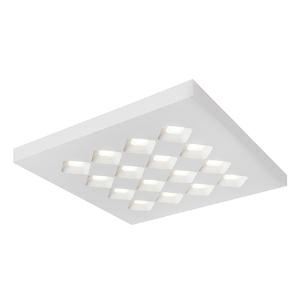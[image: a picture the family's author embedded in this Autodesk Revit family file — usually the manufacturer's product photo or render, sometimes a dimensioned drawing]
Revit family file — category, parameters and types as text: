
# Revit family: 3f_filippi_-_3f_diagon_p_soft_ugr_3f_filippi_-_12139_-_3f_diagon_p_39w-940_dali_soft_ugr_596x596
name_source: partatom
category: Lighting Fixtures
units: mm (PartAtom-declared; Revit-internal decimal feet)

## family parameters
Cut with Voids When Loaded = No
Host = Face
Light Source = No
Part Type = Normal
Room Calculation Point = No
Round Connector Dimension = Use Diameter
Shared = No

## types (1)
- 3F Filippi - 3F Dìagon P Soft UGR (1 x LED, 3890 lm, 40 W, 4000 K)
    Apparent Load = 40 VA
    Approval mark = CE
    CIE Flux Codes = 59 92 100 100 100
    Color Rendering = 90
    Color Temperature = 4000 K
    Control Gear = Electronic transformer
    Default Elevation = 1800 mm
    Description = ILLUMINOTECHNICAL
Luminous efficiency 100% (DLOR 100%, ULOR 0%).
Initial luminous flux of the luminaire 3890 lm.
Direct symmetric distribution.
Installation Interdistance Transv.D = 1.23 x hu - Long.D = 1.23 x hu.
Average luminance <3000 cd/m² for radial angles >65°.
Tabular UGR (CIE 117 - 4H-8H; S=0.25H; 70/50/20): RUG 18.9 - 18.9.
Beam angle: 102° - 101°.
Luminous efficacy 97 lm/W.
Lifetime (L90/B10): 30000 h. (tq+25°C)
Lifetime (L85/B10): 50000 h. (tq+25°C)
Lifetime (L80/B20): 80000 h. (tq+25°C)
Lifetime (L70/B20): 100000 h. (tq+25°C)
Sudden decreased luminous flux after 50000 hours: 0% (C0).
Photobiological safety in compliance with IEC/TR 62778: RG0 risk exempt, (IEC 62471).
In compliance with IEC/EN 62722-2-1 - IEC/EN 62717 standards.

SOURCE
Squared LED module 39W/940.
Energy efficiency class (UE 2019/2020 - UE 2019/2015): D.
CIE 13.3 Colour rendering index: CRI >90 (R9 >50%).
IES TM-30 Fidelity Index: Rf = 92 Rg = 101.
CCT nominal colour temperature 4000 K.
Colour initial tolerance (MacAdam): SDCM 3.

MECHANICAL
White painted frame.
Height only 40 mm.
Housing in hot-galvanised steel, painted in white polyester.
Honeycombed diagonal screen in white anti-glare polycarbonate.
Opal methacrylate (PMMA) rhomboid lenses with differentiated, engraved and prismatic surfaces for diffused, soft lighting and excellent visual comfort.
Luminaire with limited surface temperature. - D - (EN 60598-2-24)
Dimensions: 596x596 mm, height 40 mm. Weight 6.245 kg.
IP40 protection degree.
Mechanical strength to impacts IK06 (1 joule).
Glow-wire test resistance 650°C.

ELECTRICAL
Halogen Free DALI-2, PUSH-DIM, electronic wiring 230V-50/60Hz, power factor 0.97 at full load, THD <25%, constant output current, class I, 1 driver, 1 DALI addresse.
Power of the luminaire 40 W.
ENEC - CE.
SAFE FLICKER: PstLM=<1 and SVM=<0.4 (IEC TR 61547-1 and IEC TR 63158), to ensure a more comfortable and safe light.
Luminaire compliant with EN 60598-2-22 for power supply from a centralised emergency system CPSS (Central Power Supply System), not incorporated in the luminaire - high risk areas excluded. The default power and flux are 100% in AC and 15% in DC.
Ambient temperature from 0°C to +25°C.
Temperature class T6 max 85°C.
Quick connection.
Relative humidity UR: <85%.

INSTALLATION
Ceiling.

APPLICATIONS
Environments: staterooms, with VDTs, offices.
Environments with exacting visual tasks, where diffused soft light for optimum visual comfort is required.

LIGHT MANAGEMENT
Recommended minimum setting: 10%.
The device, equipped with DALI-2 driver, can be controlled manually with 3F Easy Dim technology or automatically/manually with 3F Smart Dimming technology and/or centralised DALI systems.
DALI-2 certification guarantees interoperability with other devices with the same certification.
In electrical systems without a regulation system (manual or automatic) and DALI bus, a suitable jumper must be made on the DA-DA terminals of the appliance.

WARNING
Luminaire designed for disposal/recycling at end-of-life.
Replaceable (LED only) light source by a professional. Replaceable control gear by a professional.
    Height = 40 mm  [stored 0.131234 ft]
    Lamp = 1 x LED
    Lamp Light Flux = 3890 lm
    Lamp Power = 40 W
    Lamp count = 1
    Length = 596 mm
    Lifetime = 50000 h
    Luminous efficacy = 97 lm/W
    Manufacturer = 3F Filippi
    ModVariant = No
    Model = 3F Filippi - 12139 - 3F Diagon P 39W-940 DALI SOFT UGR 596x596
    Mounting Place = Ceiling
    Mounting Type = Surface mounted
    Number of Poles = 1
    OnlyDefault = Yes
    Power Factor = 1
    Product Name = 3F Filippi - 3F Dìagon P Soft UGR
    Product group = ceiling mounted luminaire
    ProductGroupID = 3
    Protection Class = Protection class I
    Protection Degree = IP 40
    RLX_Detail_Level = 1
    RLX_Emergency_Light_Flux = 0 lm
    RLX_Emergency_Type = 0
    RLX_Emergency_Type_DB = No
    RlxData = <blob elided: 97141 chars, md5=96fe0fc0>
    Socket = socket
    Standby Power = 0 W
    System Light Flux = 3890 lm
    System Power = 40 W
    Type Comments = Product without accessories
    Type Image = 3ffilippi_3f_diagon_p_soft_ugr.jpg
    URL = http://relux.com
    VarID = ---
    Voltage = 0 V
    Weight = 0.00 kg
    Width = 596 mm

note: [stored X ft] marks values corroborated as IEEE doubles in the binary element streams (Revit-internal decimal feet)

## geometry (parser evidence)
native form markers: Blend x4, Sweep x9
no freeform markers — native parametric forms only
